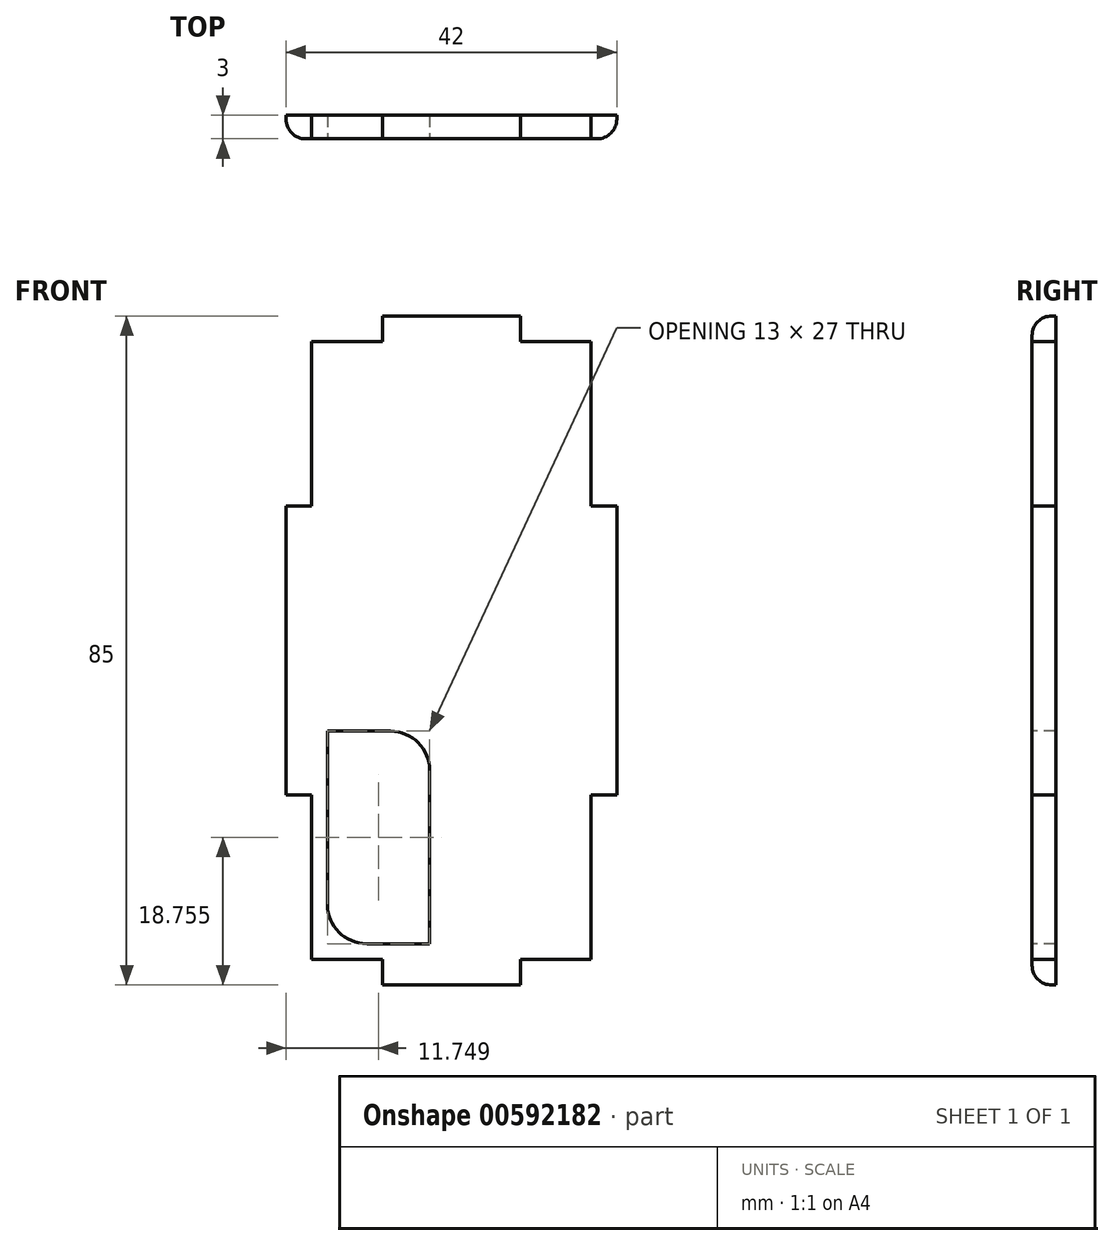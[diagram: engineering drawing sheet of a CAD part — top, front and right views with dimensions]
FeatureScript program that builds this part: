
annotation { "Feature Type Name" : "Feature", "Feature Type Description" : "" }
export const myFeature = defineFeature(function(context is Context, id is Id, definition is map)
    precondition{}
    {
        {
            var Q0;
            Q0=qCreatedBy(makeId("Front.planeOp"),FACE);
            var sketch = newSketch(context, id + "F0", { "sketchPlane" : qUnion([Q0])});
            skLineSegment(sketch, "E0.bottom", {"start": v(-33.3, 32.93) * mm, "end": v(8.7, 32.93) * mm});
            skLineSegment(sketch, "E0.top", {"start": v(-33.3, -52.07) * mm, "end": v(8.7, -52.07) * mm});
            skLineSegment(sketch, "E0.left", {"start": v(-33.3, 32.93) * mm, "end": v(-33.3, -52.07) * mm});
            skLineSegment(sketch, "E0.right", {"start": v(8.7, 32.93) * mm, "end": v(8.7, -52.07) * mm});
            skSolve(sketch);
        }
        {
            var Q0;
            Q0 = qSketchRegion(id + "F0", true);
            extrude(context, id + "F1", {"entities" : qUnion([Q0]), "depth" : 3 * mm, "offsetDistance" : 25 * mm});
        }
        {
            var Q0;
            Q0=makeQuery(id+"F1.opExtrude","SWEPT_EDGE",EDGE,{"disambiguationData":[OSD([sQuery(id+"F0.wireOp",EDGE,"E0.bottom"),sQuery(id+"F0.wireOp",EDGE,"E0.left")])]});
            var Q1;
            Q1=makeQuery(id+"F1.opExtrude","SWEPT_EDGE",EDGE,{"disambiguationData":[OSD([sQuery(id+"F0.wireOp",EDGE,"E0.bottom"),sQuery(id+"F0.wireOp",EDGE,"E0.right")])]});
            var Q2;
            Q2=makeQuery(id+"F1.opExtrude","SWEPT_EDGE",EDGE,{"disambiguationData":[OSD([sQuery(id+"F0.wireOp",EDGE,"E0.top"),sQuery(id+"F0.wireOp",EDGE,"E0.right")])]});
            var Q3;
            Q3=makeQuery(id+"F1.opExtrude","SWEPT_EDGE",EDGE,{"disambiguationData":[OSD([sQuery(id+"F0.wireOp",EDGE,"E0.top"),sQuery(id+"F0.wireOp",EDGE,"E0.left")])]});
            fillet(context, id + "F2", {"entities" : qUnion([Q0, Q1, Q2, Q3]), "tangentPropagation" : true, "radius" : 3 * mm, "defaultsChanged" : false, "vertexSettings" : [], "allowEdgeOverflow" : false});
        }
        {
            var Q0;
            Q0=makeQuery(id+"F1.opExtrude","CAP_FACE",FACE,{"disambiguationData":[OSD([sQuery(id+"F0.wireOp",EDGE,"E0.bottom"),sQuery(id+"F0.wireOp",EDGE,"E0.top"),sQuery(id+"F0.wireOp",EDGE,"E0.left"),sQuery(id+"F0.wireOp",EDGE,"E0.right")])],"isStart":true});
            var sketch = newSketch(context, id + "F3", { "sketchPlane" : qUnion([Q0])});
            skLineSegment(sketch, "E1.bottom", {"start": v(-5.46, 29.68) * mm, "end": v(30.04, 29.68) * mm});
            skLineSegment(sketch, "E1.top", {"start": v(-5.46, -48.82) * mm, "end": v(30.04, -48.82) * mm});
            skLineSegment(sketch, "E1.left", {"start": v(-5.46, 29.68) * mm, "end": v(-5.46, -48.82) * mm});
            skLineSegment(sketch, "E1.right", {"start": v(30.04, 29.68) * mm, "end": v(30.04, -48.82) * mm});
            skLineSegment(sketch, "E2", {"start": v(3.54, 32.93) * mm, "end": v(3.54, 29.68) * mm});
            skPoint(sketch, "E2.endSnap0", {"position": v(12.3, 29.68) * mm});
            skLineSegment(sketch, "E3", {"start": v(3.54, 29.68) * mm, "end": v(21.04, 29.68) * mm});
            skLineSegment(sketch, "E4", {"start": v(21.04, 29.68) * mm, "end": v(21.04, 32.93) * mm});
            skLineSegment(sketch, "E5", {"start": v(21.04, 32.93) * mm, "end": v(3.54, 32.93) * mm});
            skLineSegment(sketch, "E6", {"start": v(3.54, -48.82) * mm, "end": v(3.54, -52.07) * mm});
            skLineSegment(sketch, "E7", {"start": v(3.54, -52.07) * mm, "end": v(21.04, -52.07) * mm});
            skLineSegment(sketch, "E8", {"start": v(21.04, -52.07) * mm, "end": v(21.04, -48.82) * mm});
            skLineSegment(sketch, "E9", {"start": v(21.04, -48.82) * mm, "end": v(3.54, -48.82) * mm});
            skLineSegment(sketch, "E10", {"start": v(-8.7, 8.76) * mm, "end": v(-5.46, 8.76) * mm});
            skLineSegment(sketch, "E11", {"start": v(-5.46, 8.76) * mm, "end": v(-5.46, -27.9) * mm});
            skLineSegment(sketch, "E12", {"start": v(-5.46, -27.9) * mm, "end": v(-8.7, -27.9) * mm});
            skLineSegment(sketch, "E13", {"start": v(-8.7, -27.9) * mm, "end": v(-8.7, 8.76) * mm});
            skLineSegment(sketch, "E14", {"start": v(30.04, 8.76) * mm, "end": v(33.3, 8.76) * mm});
            skLineSegment(sketch, "E15", {"start": v(33.3, 8.76) * mm, "end": v(33.3, -27.9) * mm});
            skLineSegment(sketch, "E16", {"start": v(33.3, -27.9) * mm, "end": v(30.04, -27.9) * mm});
            skLineSegment(sketch, "E17", {"start": v(30.04, -27.9) * mm, "end": v(30.04, 8.76) * mm});
            skSolve(sketch);
        }
        {
            var Q0;
            {var subQ1=sQuery(id+"F3.wireOp",EDGE,"E2");Q0=makeQuery(id+"F3.imprint","IMPRINT",FACE,{"disambiguationData":[TD([[makeQuery(id+"F3.imprint","IMPRINT",EDGE,{"derivedFrom":subQ1}),-1.0]])]});}
            var Q1;
            {var subQ1=sQuery(id+"F3.wireOp",EDGE,"E4");Q1=makeQuery(id+"F3.imprint","IMPRINT",FACE,{"disambiguationData":[TD([[makeQuery(id+"F3.imprint","IMPRINT",EDGE,{"derivedFrom":subQ1}),-1.0]])]});}
            var Q2;
            {var subQ0=sQuery(id+"F3.wireOp",EDGE,"E8");Q2=makeQuery(id+"F3.imprint","IMPRINT",FACE,{"disambiguationData":[TD([[makeQuery(id+"F3.imprint","IMPRINT",EDGE,{"derivedFrom":subQ0}),-1.0]])]});}
            var Q3;
            {var subQ7=sQuery(id+"F3.wireOp",EDGE,"E6");Q3=makeQuery(id+"F3.imprint","IMPRINT",FACE,{"disambiguationData":[TD([[makeQuery(id+"F3.imprint","IMPRINT",EDGE,{"derivedFrom":subQ7}),-1.0]])]});}
            extrude(context, id + "F4", {"entities" : qUnion([Q0, Q1, Q2, Q3]), "operationType" : NewBodyOperationType.REMOVE, "endBound" : BoundingType.UP_TO_NEXT, "oppositeDirection" : true, "depth" : 25 * mm, "offsetDistance" : 25 * mm});
        }
        {
            var Q0;
            Q0=makeQuery(id+"F1.opExtrude","CAP_FACE",FACE,{"disambiguationData":[OSD([sQuery(id+"F0.wireOp",EDGE,"E0.bottom"),sQuery(id+"F0.wireOp",EDGE,"E0.top"),sQuery(id+"F0.wireOp",EDGE,"E0.left"),sQuery(id+"F0.wireOp",EDGE,"E0.right")])],"isStart":false});
            var sketch = newSketch(context, id + "F5", { "sketchPlane" : qUnion([Q0])});
            skLineSegment(sketch, "E18.bottom", {"start": v(-28.04, -19.82) * mm, "end": v(-15.04, -19.82) * mm});
            skLineSegment(sketch, "E18.top", {"start": v(-28.04, -46.82) * mm, "end": v(-15.04, -46.82) * mm});
            skLineSegment(sketch, "E18.left", {"start": v(-28.04, -19.82) * mm, "end": v(-28.04, -46.82) * mm});
            skLineSegment(sketch, "E18.right", {"start": v(-15.04, -19.82) * mm, "end": v(-15.04, -46.82) * mm});
            skSolve(sketch);
        }
        {
            var Q0;
            Q0=makeQuery(id+"F5.imprint","IMPRINT",FACE,{"disambiguationData":[TD([[makeQuery(id+"F5.imprint","IMPRINT",EDGE,{"derivedFrom":sQuery(id+"F5.wireOp",EDGE,"E18.bottom")}),-1.0]])]});
            extrude(context, id + "F6", {"entities" : qUnion([Q0]), "operationType" : NewBodyOperationType.REMOVE, "endBound" : BoundingType.UP_TO_NEXT, "oppositeDirection" : true, "depth" : 25 * mm, "offsetDistance" : 25 * mm});
        }
        {
            var Q0;
            Q0=makeQuery(id+"F6.boolean.opBoolean","COPY",EDGE,{"derivedFrom":makeQuery(id+"F6.opExtrude","SWEPT_EDGE",EDGE,{"disambiguationData":[OSD([sQuery(id+"F5.wireOp",EDGE,"E18.bottom"),sQuery(id+"F5.wireOp",EDGE,"E18.right")])]})});
            var Q1;
            Q1=makeQuery(id+"F6.boolean.opBoolean","COPY",EDGE,{"derivedFrom":makeQuery(id+"F6.opExtrude","SWEPT_EDGE",EDGE,{"disambiguationData":[OSD([sQuery(id+"F5.wireOp",EDGE,"E18.top"),sQuery(id+"F5.wireOp",EDGE,"E18.left")])]})});
            fillet(context, id + "F7", {"entities" : qUnion([Q0, Q1]), "tangentPropagation" : true, "radius" : 5 * mm, "defaultsChanged" : false, "vertexSettings" : [], "allowEdgeOverflow" : false});
        }
        {
            var Q0;
            Q0=makeQuery(id+"F1.opExtrude","CAP_EDGE",EDGE,{"disambiguationData":[OSD([sQuery(id+"F0.wireOp",EDGE,"E0.bottom")])],"isStart":false});
            var Q1;
            Q1=makeQuery(id+"F1.opExtrude","CAP_EDGE",EDGE,{"disambiguationData":[OSD([sQuery(id+"F0.wireOp",EDGE,"E0.right")])],"isStart":false});
            var Q2;
            Q2=makeQuery(id+"F1.opExtrude","CAP_EDGE",EDGE,{"disambiguationData":[OSD([sQuery(id+"F0.wireOp",EDGE,"E0.top")])],"isStart":false});
            var Q3;
            Q3=makeQuery(id+"F1.opExtrude","CAP_EDGE",EDGE,{"disambiguationData":[OSD([sQuery(id+"F0.wireOp",EDGE,"E0.left")])],"isStart":false});
            fillet(context, id + "F8", {"entities" : qUnion([Q0, Q1, Q2, Q3]), "tangentPropagation" : true, "radius" : 2.5 * mm, "defaultsChanged" : false, "vertexSettings" : [], "allowEdgeOverflow" : false});
        }
    });
